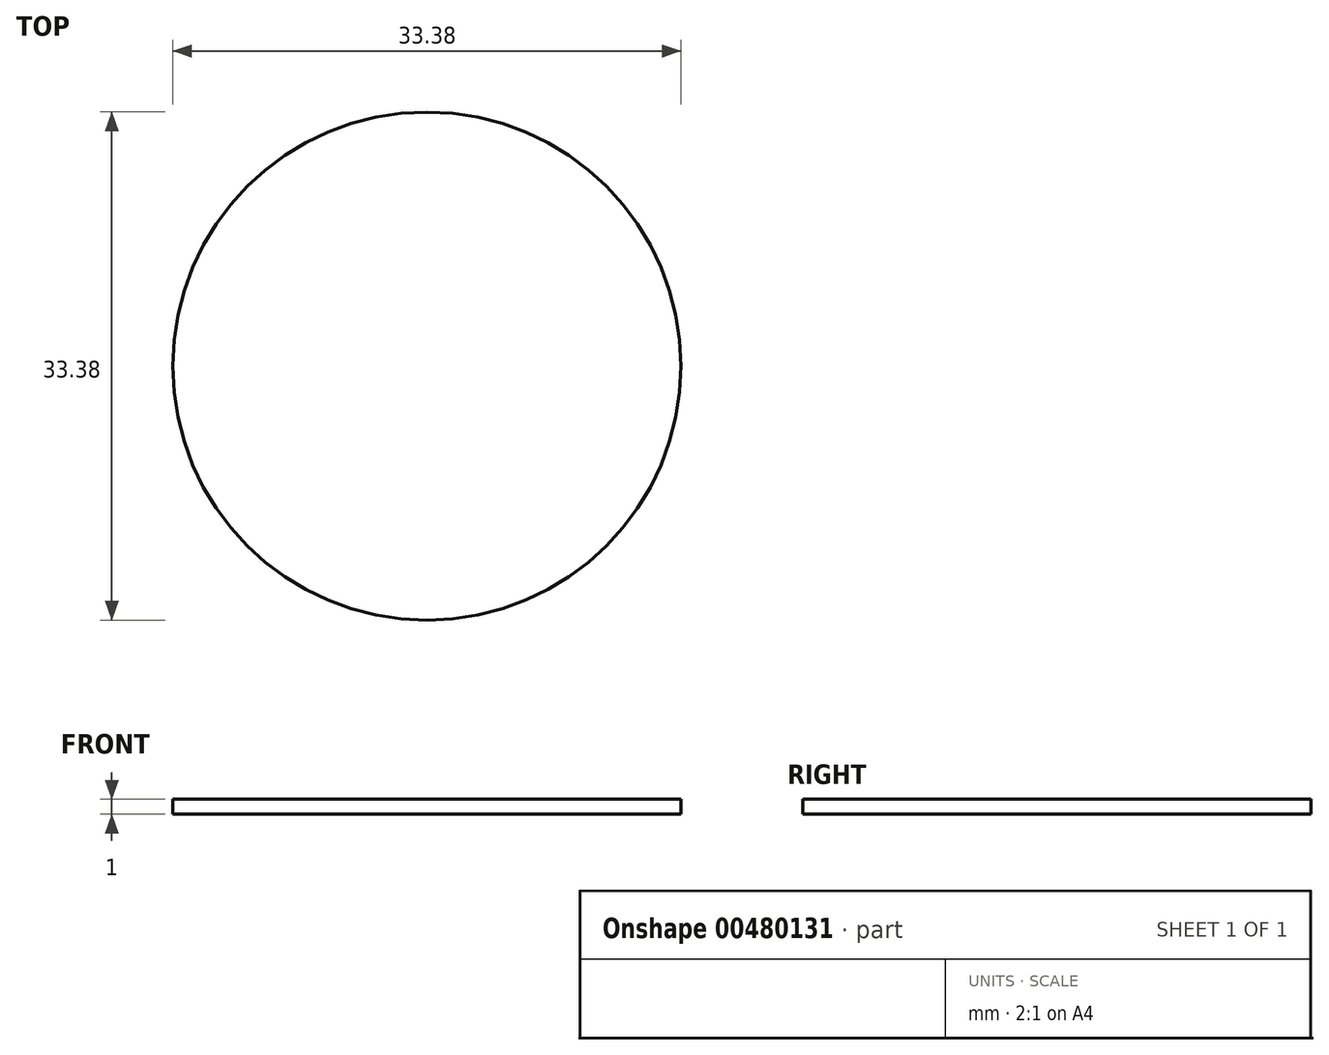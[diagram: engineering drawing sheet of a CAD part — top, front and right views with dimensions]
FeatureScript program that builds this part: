
annotation { "Feature Type Name" : "Feature", "Feature Type Description" : "" }
export const myFeature = defineFeature(function(context is Context, id is Id, definition is map)
    precondition{}
    {
        {
            var Q0;
            Q0=qCreatedBy(makeId("Top.planeOp"),FACE);
            var sketch = newSketch(context, id + "F0", { "sketchPlane" : qUnion([Q0])});
            skCircle(sketch, "E0", {"center": v(0, 0) * mm, "radius": 16.69 * mm});
            skSolve(sketch);
        }
        {
            var Q0;
            Q0 = qSketchRegion(id + "F0", true);
            extrude(context, id + "F1", {"entities" : qUnion([Q0]), "depth" : 1 * mm});
        }
    });
